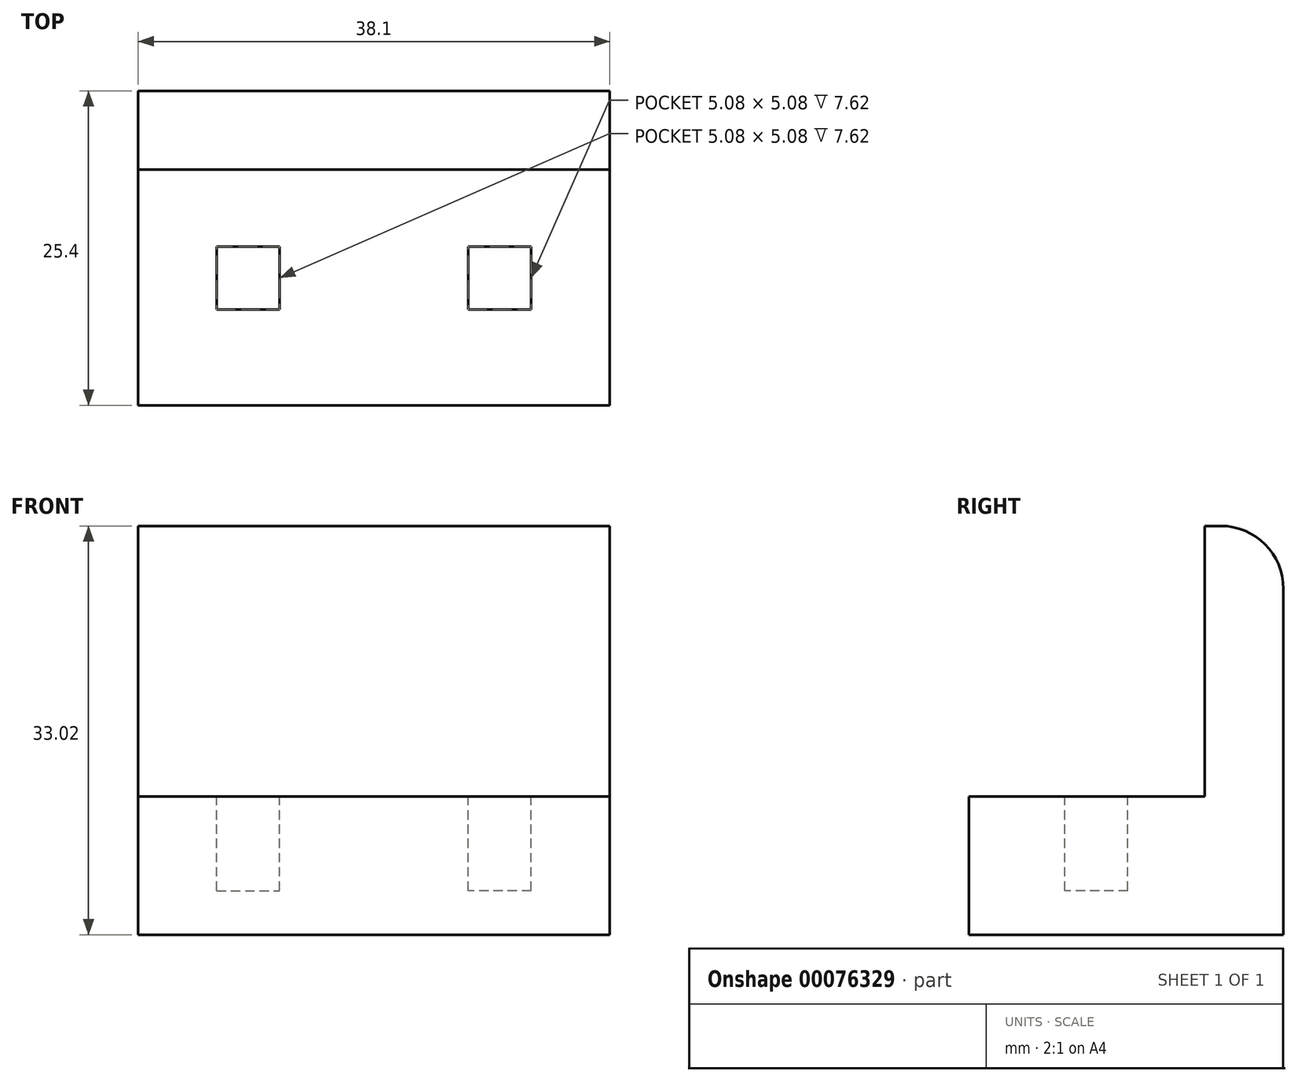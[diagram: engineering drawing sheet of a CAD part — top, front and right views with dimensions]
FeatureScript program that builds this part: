
annotation { "Feature Type Name" : "Feature", "Feature Type Description" : "" }
export const myFeature = defineFeature(function(context is Context, id is Id, definition is map)
    precondition{}
    {
        {
            var Q0;
            Q0=qCreatedBy(makeId("Front.planeOp"),FACE);
            var sketch = newSketch(context, id + "F0", { "sketchPlane" : qUnion([Q0])});
            skLineSegment(sketch, "E0.bottom", {"start": v(0, 0) * mm, "end": v(38.1, 0) * mm});
            skLineSegment(sketch, "E0.top", {"start": v(0, 33.02) * mm, "end": v(38.1, 33.02) * mm});
            skLineSegment(sketch, "E0.left", {"start": v(0, 0) * mm, "end": v(0, 33.02) * mm});
            skLineSegment(sketch, "E0.right", {"start": v(38.1, 0) * mm, "end": v(38.1, 33.02) * mm});
            skSolve(sketch);
        }
        {
            var Q0;
            Q0=makeQuery(id+"F0.imprint","IMPRINT",FACE,{"disambiguationData":[TD([[makeQuery(id+"F0.imprint","IMPRINT",EDGE,{"derivedFrom":sQuery(id+"F0.wireOp",EDGE,"E0.bottom")}),1.0]])]});
            extrude(context, id + "F1", {"entities" : qUnion([Q0]), "depth" : 25.4 * mm});
        }
        {
            var Q0;
            Q0=makeQuery(id+"F1.opExtrude","CAP_FACE",FACE,{"disambiguationData":[OSD([sQuery(id+"F0.wireOp",EDGE,"E0.bottom"),sQuery(id+"F0.wireOp",EDGE,"E0.top"),sQuery(id+"F0.wireOp",EDGE,"E0.left"),sQuery(id+"F0.wireOp",EDGE,"E0.right")])],"isStart":false});
            var sketch = newSketch(context, id + "F2", { "sketchPlane" : qUnion([Q0])});
            skLineSegment(sketch, "E1.bottom", {"start": v(0, 33.02) * mm, "end": v(38.1, 33.02) * mm});
            skLineSegment(sketch, "E1.top", {"start": v(0, 11.18) * mm, "end": v(38.1, 11.18) * mm});
            skLineSegment(sketch, "E1.left", {"start": v(0, 33.02) * mm, "end": v(0, 11.18) * mm});
            skLineSegment(sketch, "E1.right", {"start": v(38.1, 33.02) * mm, "end": v(38.1, 11.18) * mm});
            skSolve(sketch);
        }
        {
            var Q0;
            Q0=makeQuery(id+"F2.imprint","IMPRINT",FACE,{"disambiguationData":[TD([[makeQuery(id+"F2.imprint","IMPRINT",EDGE,{"derivedFrom":sQuery(id+"F2.wireOp",EDGE,"E1.bottom")}),-1.0]])]});
            extrude(context, id + "F3", {"entities" : qUnion([Q0]), "operationType" : NewBodyOperationType.REMOVE, "oppositeDirection" : true, "depth" : 19.05 * mm});
        }
        {
            var Q0;
            Q0=makeQuery(id+"F3.boolean.opBoolean","COPY",FACE,{"derivedFrom":makeQuery(id+"F3.opExtrude","SWEPT_FACE",FACE,{"disambiguationData":[OSD([sQuery(id+"F2.wireOp",EDGE,"E1.top")])]})});
            var sketch = newSketch(context, id + "F4", { "sketchPlane" : qUnion([Q0])});
            skLineSegment(sketch, "E2", {"start": v(19.05, -6.35) * mm, "end": v(19.05, -25.4) * mm});
            skLineSegment(sketch, "E3.bottom", {"start": v(6.35, -12.57) * mm, "end": v(11.43, -12.57) * mm});
            skLineSegment(sketch, "E3.top", {"start": v(6.35, -17.65) * mm, "end": v(11.43, -17.65) * mm});
            skLineSegment(sketch, "E3.left", {"start": v(6.35, -12.57) * mm, "end": v(6.35, -17.65) * mm});
            skLineSegment(sketch, "E3.right", {"start": v(11.43, -12.57) * mm, "end": v(11.43, -17.65) * mm});
            skLineSegment(sketch, "E4.MirrorCS", {"start": v(26.67, -12.57) * mm, "end": v(26.67, -17.65) * mm});
            skLineSegment(sketch, "E5.MirrorCS", {"start": v(31.75, -12.57) * mm, "end": v(26.67, -12.57) * mm});
            skLineSegment(sketch, "E6.MirrorCS", {"start": v(31.75, -12.57) * mm, "end": v(31.75, -17.65) * mm});
            skLineSegment(sketch, "E7.MirrorCS", {"start": v(31.75, -17.65) * mm, "end": v(26.67, -17.65) * mm});
            skSolve(sketch);
        }
        {
            var Q0;
            Q0=makeQuery(id+"F4.imprint","IMPRINT",FACE,{"disambiguationData":[TD([[makeQuery(id+"F4.imprint","IMPRINT",EDGE,{"derivedFrom":sQuery(id+"F4.wireOp",EDGE,"E3.bottom")}),-1.0]])]});
            var Q1;
            Q1=makeQuery(id+"F4.imprint","IMPRINT",FACE,{"disambiguationData":[TD([[makeQuery(id+"F4.imprint","IMPRINT",EDGE,{"derivedFrom":sQuery(id+"F4.wireOp",EDGE,"E4.MirrorCS")}),1.0]])]});
            extrude(context, id + "F5", {"entities" : qUnion([Q0, Q1]), "operationType" : NewBodyOperationType.REMOVE, "oppositeDirection" : true, "depth" : 7.62 * mm});
        }
        {
            var Q0;
            Q0=makeQuery(id+"F1.opExtrude","CAP_EDGE",EDGE,{"disambiguationData":[OSD([sQuery(id+"F0.wireOp",EDGE,"E0.top")])],"isStart":true});
            fillet(context, id + "F6", {"entities" : qUnion([Q0]), "radius" : 5.08 * mm, "tangentPropagation" : true, "allowEdgeOverflow" : false});
        }
    });
